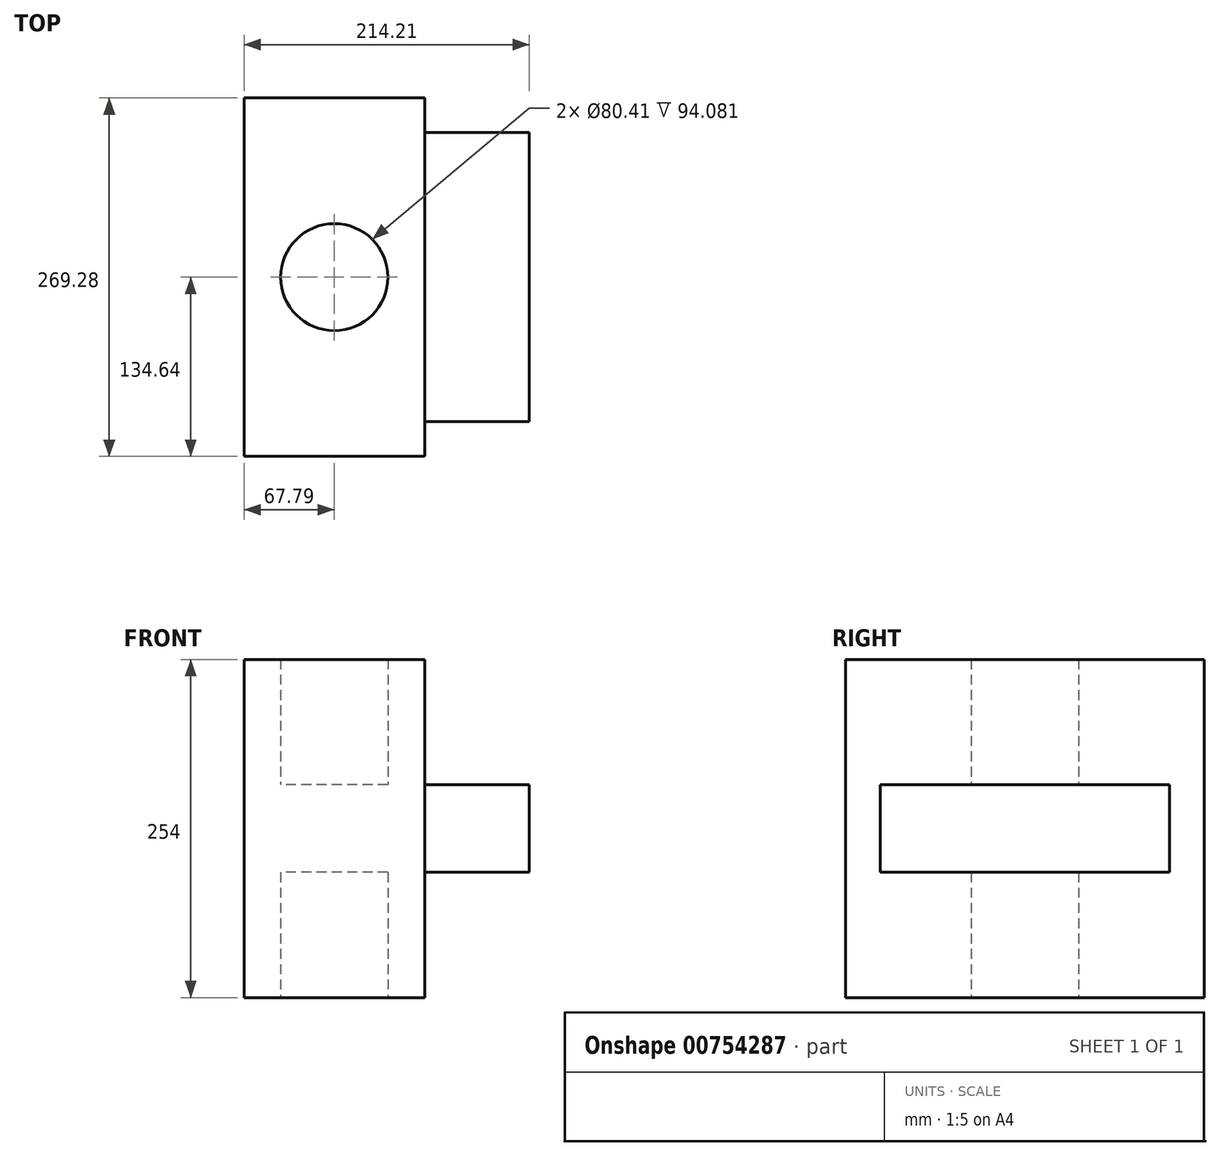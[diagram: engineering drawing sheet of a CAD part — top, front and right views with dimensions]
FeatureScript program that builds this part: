
annotation { "Feature Type Name" : "Feature", "Feature Type Description" : "" }
export const myFeature = defineFeature(function(context is Context, id is Id, definition is map)
    precondition{}
    {
        {
            var Q0;
            Q0=qCreatedBy(makeId("Top.planeOp"),FACE);
            var sketch = newSketch(context, id + "F0", { "sketchPlane" : qUnion([Q0])});
            skLineSegment(sketch, "E0.bottom", {"start": v(-67.8, 134.64) * mm, "end": v(67.8, 134.64) * mm});
            skLineSegment(sketch, "E0.top", {"start": v(-67.8, -134.64) * mm, "end": v(67.8, -134.64) * mm});
            skLineSegment(sketch, "E0.left", {"start": v(-67.8, 134.64) * mm, "end": v(-67.8, -134.64) * mm});
            skLineSegment(sketch, "E0.right", {"start": v(67.8, 134.64) * mm, "end": v(67.8, -134.64) * mm});
            skPoint(sketch, "E0.middle", {"position": v(0, 0) * mm});
            skCircle(sketch, "E1", {"center": v(0, 0) * mm, "radius": 40.2 * mm});
            skSolve(sketch);
        }
        {
            var Q0;
            Q0 = qSketchRegion(id + "F0", true);
            var sketch = newSketch(context, id + "F1", { "sketchPlane" : qUnion([Q0])});
            skSolve(sketch);
        }
        {
            var Q0;
            Q0=makeQuery(id+"F1.imprint","IMPRINT",FACE,{"disambiguationData":[TD([[makeQuery(id+"F1.imprint","IMPRINT",EDGE,{"derivedFrom":makeQuery(id+"F0.imprint","IMPRINT",EDGE,{"derivedFrom":sQuery(id+"F0.wireOp",EDGE,"E0.bottom")})}),-1.0]])]});
            extrude(context, id + "F2", {"entities" : qUnion([Q0]), "depth" : 254 * mm, "offsetDistance" : 25.4 * mm});
        }
        {
            var Q0;
            Q0=makeQuery(id+"F2.opExtrude","SWEPT_FACE",FACE,{"disambiguationData":[OSD([sQuery(id+"F0.wireOp",EDGE,"E0.left")])]});
            var sketch = newSketch(context, id + "F3", { "sketchPlane" : qUnion([Q0])});
            skLineSegment(sketch, "E2.bottom", {"start": v(108.58, 159.92) * mm, "end": v(-108.58, 159.92) * mm});
            skLineSegment(sketch, "E2.top", {"start": v(108.58, 94.08) * mm, "end": v(-108.58, 94.08) * mm});
            skLineSegment(sketch, "E2.left", {"start": v(108.58, 159.92) * mm, "end": v(108.58, 94.08) * mm});
            skLineSegment(sketch, "E2.right", {"start": v(-108.58, 159.92) * mm, "end": v(-108.58, 94.08) * mm});
            skPoint(sketch, "E2.middle", {"position": v(0, 127) * mm});
            skPoint(sketch, "E2.middle.positionSnap0", {"position": v(134.64, 127) * mm});
            skPoint(sketch, "E2.centerSnap0", {"position": v(134.64, 127) * mm});
            skSolve(sketch);
        }
        {
            var Q0;
            Q0 = qSketchRegion(id + "F3", true);
            extrude(context, id + "F4", {"entities" : qUnion([Q0]), "operationType" : NewBodyOperationType.ADD, "oppositeDirection" : true, "depth" : 214.2 * mm, "offsetDistance" : 25.4 * mm});
        }
    });
